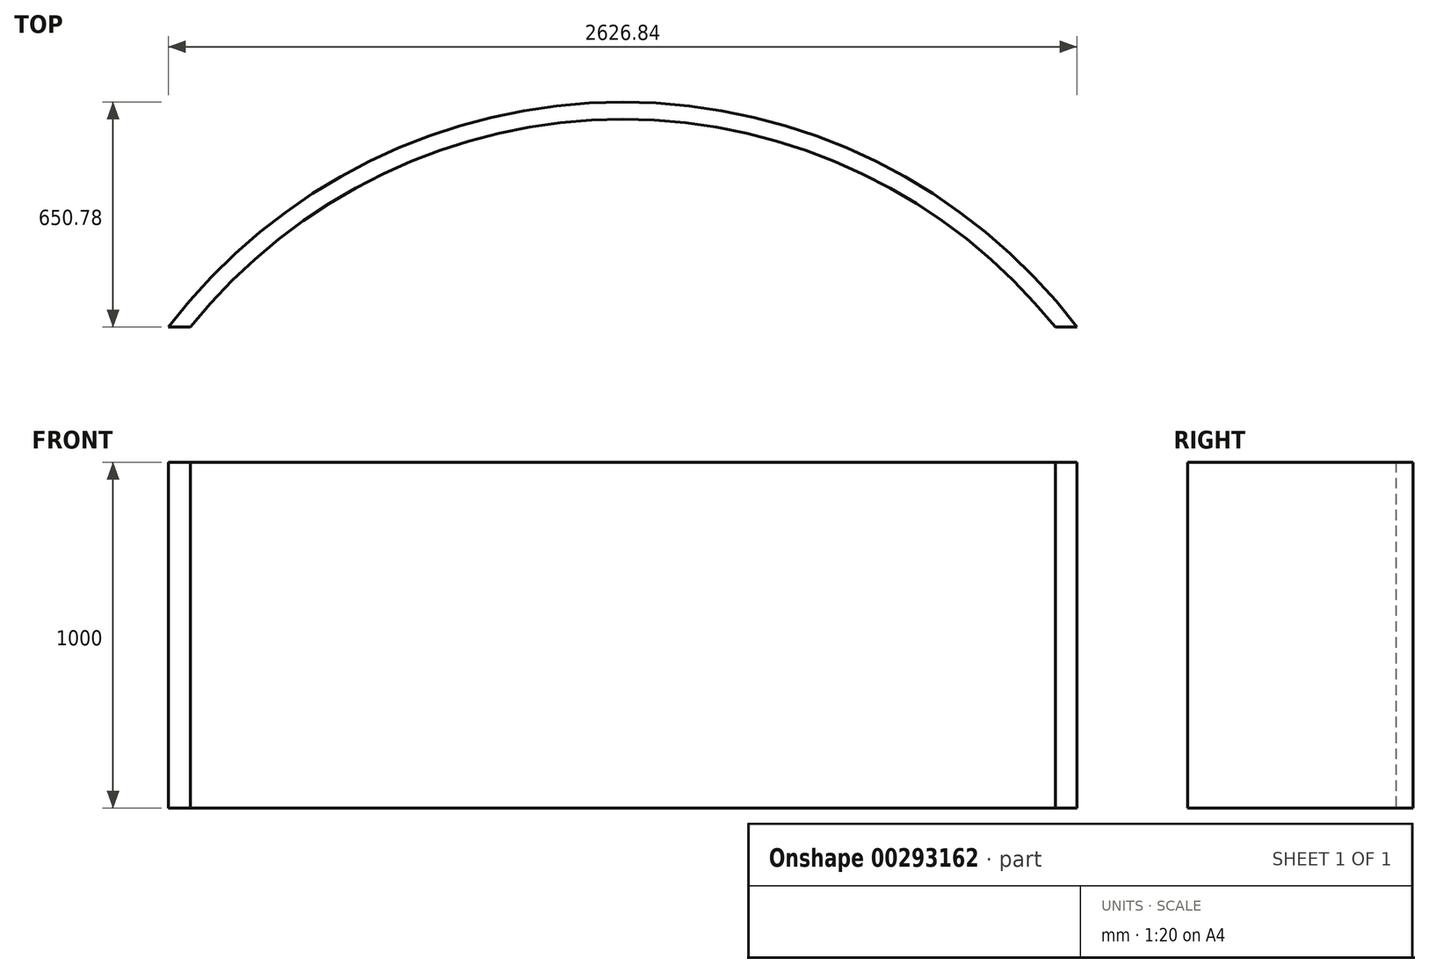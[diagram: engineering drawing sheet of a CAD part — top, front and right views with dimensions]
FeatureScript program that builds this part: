
annotation { "Feature Type Name" : "Feature", "Feature Type Description" : "" }
export const myFeature = defineFeature(function(context is Context, id is Id, definition is map)
    precondition{}
    {
        {
            var Q0;
            Q0=qCreatedBy(makeId("Top.planeOp"),FACE);
            var sketch = newSketch(context, id + "F0", { "sketchPlane" : qUnion([Q0])});
            skLineSegment(sketch, "E0", {"start": v(0, 0) * mm, "end": v(0, 600.78) * mm, "construction": true});
            skArc(sketch, "E1", {"start": v(1250, 0) * mm, "mid": v(0, 600.78) * mm, "end": v(-1250, 0) * mm});
            skArc(sketch, "E2", {"start": v(1313.42, 0) * mm, "mid": v(0, 650.78) * mm, "end": v(-1313.42, 0) * mm});
            skLineSegment(sketch, "E3", {"start": v(-1313.42, 0) * mm, "end": v(-1250, 0) * mm});
            skLineSegment(sketch, "E4", {"start": v(1313.42, 0) * mm, "end": v(1250, 0) * mm});
            skSolve(sketch);
        }
        {
            var Q0;
            Q0=makeQuery(id+"F0.imprint","IMPRINT",FACE,{"disambiguationData":[TD([[makeQuery(id+"F0.imprint","IMPRINT",EDGE,{"derivedFrom":sQuery(id+"F0.wireOp",EDGE,"E1")}),-1.0]])]});
            var Q1;
            Q1=sQuery(id+"F0.wireOp",EDGE,"E1");
            extrude(context, id + "F1", {"entities" : qUnion([Q0]), "surfaceEntities" : qUnion([Q1]), "depth" : 1000 * mm});
        }
    });
